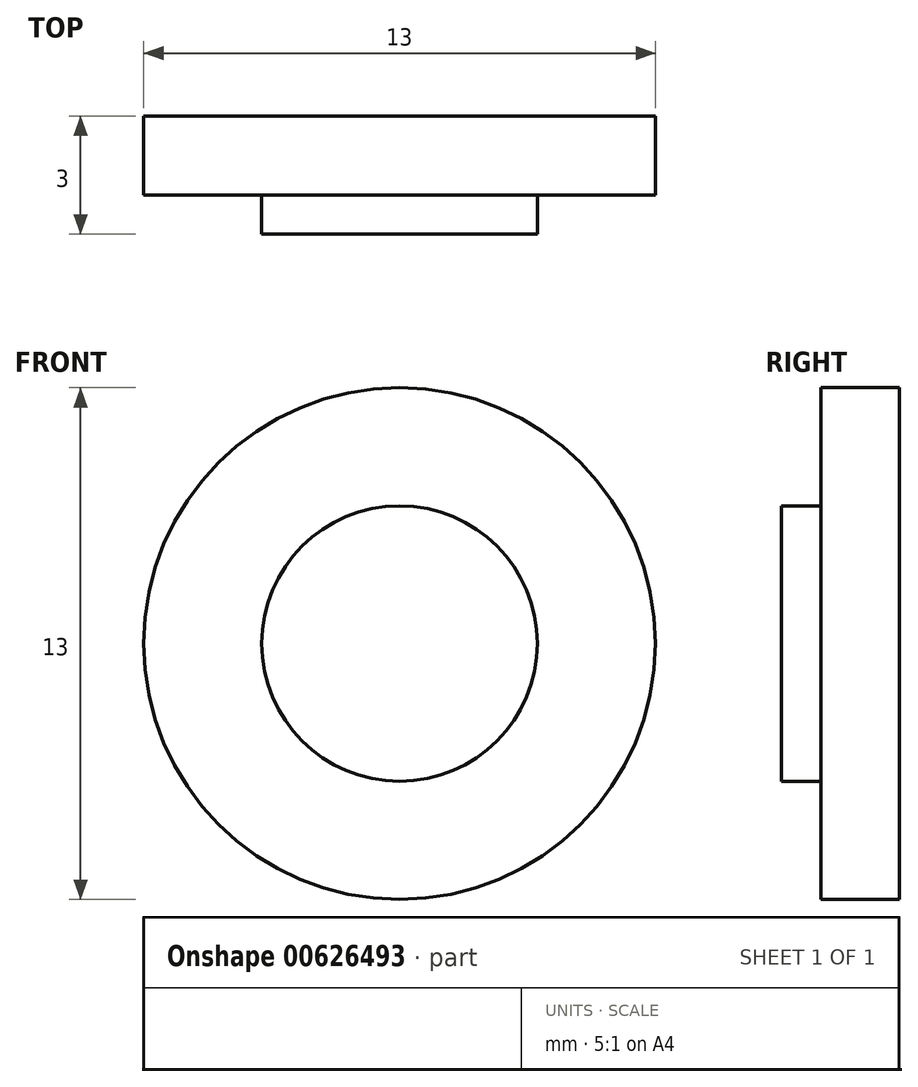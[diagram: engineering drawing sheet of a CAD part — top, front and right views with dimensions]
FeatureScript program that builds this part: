
annotation { "Feature Type Name" : "Feature", "Feature Type Description" : "" }
export const myFeature = defineFeature(function(context is Context, id is Id, definition is map)
    precondition{}
    {
        {
            var Q0;
            Q0=qCreatedBy(makeId("Front.planeOp"),FACE);
            var sketch = newSketch(context, id + "F0", { "sketchPlane" : qUnion([Q0])});
            skCircle(sketch, "E0", {"center": v(0, 0) * mm, "radius": 6.5 * mm});
            skCircle(sketch, "E1", {"center": v(0, 0) * mm, "radius": 3.5 * mm});
            skSolve(sketch);
        }
        {
            var Q0;
            Q0=makeQuery(id+"F0.imprint","IMPRINT",FACE,{"disambiguationData":[TD([[makeQuery(id+"F0.imprint","IMPRINT",EDGE,{"derivedFrom":sQuery(id+"F0.wireOp",EDGE,"E0")}),1.0]])]});
            var Q1;
            Q1=makeQuery(id+"F0.imprint","IMPRINT",FACE,{"disambiguationData":[TD([[makeQuery(id+"F0.imprint","IMPRINT",EDGE,{"derivedFrom":sQuery(id+"F0.wireOp",EDGE,"E1")}),1.0]])]});
            extrude(context, id + "F1", {"entities" : qUnion([Q0, Q1]), "oppositeDirection" : true, "depth" : 2 * mm, "offsetDistance" : 25 * mm});
        }
        {
            var Q0;
            Q0=makeQuery(id+"F0.imprint","IMPRINT",FACE,{"disambiguationData":[TD([[makeQuery(id+"F0.imprint","IMPRINT",EDGE,{"derivedFrom":sQuery(id+"F0.wireOp",EDGE,"E1")}),1.0]])]});
            extrude(context, id + "F2", {"entities" : qUnion([Q0]), "depth" : 1 * mm, "offsetDistance" : 25 * mm});
        }
    });
